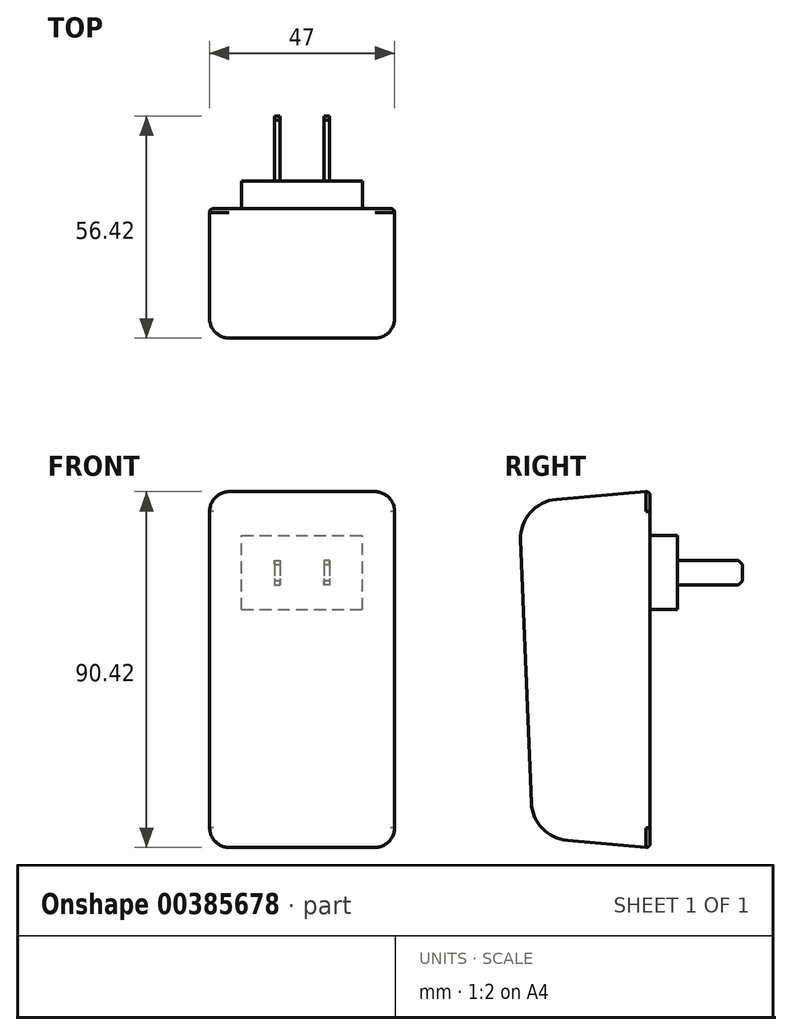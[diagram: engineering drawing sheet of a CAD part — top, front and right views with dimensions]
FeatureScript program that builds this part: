
annotation { "Feature Type Name" : "Feature", "Feature Type Description" : "" }
export const myFeature = defineFeature(function(context is Context, id is Id, definition is map)
    precondition{}
    {
        {
            var Q0;
            Q0=qCreatedBy(makeId("Right.planeOp"),FACE);
            var sketch = newSketch(context, id + "F0", { "sketchPlane" : qUnion([Q0])});
            skLineSegment(sketch, "E0", {"start": v(0, 90.6) * mm, "end": v(0, 0) * mm});
            skLineSegment(sketch, "E1", {"start": v(0, 90.6) * mm, "end": v(-33.3, 87.73) * mm});
            skLineSegment(sketch, "E2", {"start": v(-33.3, 87.73) * mm, "end": v(-29.8, 2.66) * mm});
            skLineSegment(sketch, "E3", {"start": v(-29.8, 2.66) * mm, "end": v(0, 0) * mm});
            skSolve(sketch);
        }
        {
            var Q0;
            Q0 = qSketchRegion(id + "F0", true);
            extrude(context, id + "F1", {"entities" : qUnion([Q0]), "depth" : 47 * mm, "symmetric" : true});
        }
        {
            var Q0;
            Q0=qCreatedBy(makeId("Front.planeOp"),FACE);
            var sketch = newSketch(context, id + "F2", { "sketchPlane" : qUnion([Q0])});
            skLineSegment(sketch, "E4", {"start": v(0, 0) * mm, "end": v(0, 19.9) * mm, "construction": true});
            skLineSegment(sketch, "E5.bottom", {"start": v(-15.37, 60.55) * mm, "end": v(15.37, 60.55) * mm});
            skLineSegment(sketch, "E5.top", {"start": v(-15.38, 79.35) * mm, "end": v(15.37, 79.35) * mm});
            skLineSegment(sketch, "E5.left", {"start": v(-15.37, 60.55) * mm, "end": v(-15.38, 79.35) * mm});
            skLineSegment(sketch, "E5.right", {"start": v(15.37, 60.55) * mm, "end": v(15.37, 79.35) * mm});
            skPoint(sketch, "E5.middle", {"position": v(0, 69.95) * mm});
            skLineSegment(sketch, "E6.bottom", {"start": v(-6.97, 73.05) * mm, "end": v(-5.57, 73.05) * mm});
            skLineSegment(sketch, "E6.top", {"start": v(-6.96, 66.84) * mm, "end": v(-5.57, 66.84) * mm});
            skLineSegment(sketch, "E6.left", {"start": v(-6.97, 73.05) * mm, "end": v(-6.97, 66.84) * mm});
            skLineSegment(sketch, "E6.right", {"start": v(-5.57, 73.05) * mm, "end": v(-5.57, 66.84) * mm});
            skPoint(sketch, "E6.middle", {"position": v(-6.26, 69.95) * mm});
            skLineSegment(sketch, "E7.MirrorCS", {"start": v(5.57, 73.05) * mm, "end": v(5.57, 66.84) * mm});
            skLineSegment(sketch, "E8.MirrorCS", {"start": v(6.96, 73.05) * mm, "end": v(6.96, 66.84) * mm});
            skLineSegment(sketch, "E9.MirrorCS", {"start": v(6.96, 66.84) * mm, "end": v(5.57, 66.84) * mm});
            skLineSegment(sketch, "E10.MirrorCS", {"start": v(6.97, 73.05) * mm, "end": v(5.57, 73.05) * mm});
            skPoint(sketch, "E11.MirrorP", {"position": v(6.26, 69.95) * mm});
            skSolve(sketch);
        }
        {
            var Q0;
            Q0=makeQuery(id+"F2.imprint","IMPRINT",FACE,{"disambiguationData":[TD([[makeQuery(id+"F2.imprint","IMPRINT",EDGE,{"derivedFrom":sQuery(id+"F2.wireOp",EDGE,"E7.MirrorCS")}),1.0]])]});
            var Q1;
            Q1=makeQuery(id+"F2.imprint","IMPRINT",FACE,{"disambiguationData":[TD([[makeQuery(id+"F2.imprint","IMPRINT",EDGE,{"derivedFrom":sQuery(id+"F2.wireOp",EDGE,"E6.bottom")}),-1.0]])]});
            var Q2;
            Q2=makeQuery(id+"F2.imprint","IMPRINT",FACE,{"disambiguationData":[TD([[makeQuery(id+"F2.imprint","IMPRINT",EDGE,{"derivedFrom":sQuery(id+"F2.wireOp",EDGE,"E5.bottom")}),1.0]])]});
            extrude(context, id + "F3", {"entities" : qUnion([Q0, Q1, Q2]), "operationType" : NewBodyOperationType.ADD, "oppositeDirection" : true, "depth" : 7 * mm});
        }
        {
            var Q0;
            Q0=makeQuery(id+"F2.imprint","IMPRINT",FACE,{"disambiguationData":[TD([[makeQuery(id+"F2.imprint","IMPRINT",EDGE,{"derivedFrom":sQuery(id+"F2.wireOp",EDGE,"E6.bottom")}),-1.0]])]});
            var Q1;
            Q1=makeQuery(id+"F2.imprint","IMPRINT",FACE,{"disambiguationData":[TD([[makeQuery(id+"F2.imprint","IMPRINT",EDGE,{"derivedFrom":sQuery(id+"F2.wireOp",EDGE,"E7.MirrorCS")}),1.0]])]});
            extrude(context, id + "F4", {"entities" : qUnion([Q0, Q1]), "operationType" : NewBodyOperationType.ADD, "oppositeDirection" : true, "depth" : 23.5 * mm});
        }
        {
            var Q0;
            Q0=makeQuery(id+"F1.opExtrude","SWEPT_EDGE",EDGE,{"disambiguationData":[OSD([sQuery(id+"F0.wireOp",EDGE,"E1"),sQuery(id+"F0.wireOp",EDGE,"E2")])]});
            var Q1;
            Q1=makeQuery(id+"F1.opExtrude","SWEPT_EDGE",EDGE,{"disambiguationData":[OSD([sQuery(id+"F0.wireOp",EDGE,"E2"),sQuery(id+"F0.wireOp",EDGE,"E3")])]});
            fillet(context, id + "F5", {"entities" : qUnion([Q0, Q1]), "radius" : 10 * mm, "tangentPropagation" : true, "allowEdgeOverflow" : false});
        }
        {
            var Q0;
            Q0=makeQuery(id+"F1.opExtrude","CAP_EDGE",EDGE,{"disambiguationData":[OSD([sQuery(id+"F0.wireOp",EDGE,"E2")])],"isStart":false});
            var Q1;
            Q1=makeQuery(id+"F1.opExtrude","CAP_EDGE",EDGE,{"disambiguationData":[OSD([sQuery(id+"F0.wireOp",EDGE,"E2")])],"isStart":true});
            fillet(context, id + "F6", {"entities" : qUnion([Q0, Q1]), "radius" : 5 * mm, "tangentPropagation" : true, "allowEdgeOverflow" : false});
        }
        {
            var Q0;
            Q0=makeQuery(id+"F1.opExtrude","CAP_EDGE",EDGE,{"disambiguationData":[OSD([sQuery(id+"F0.wireOp",EDGE,"E0")])],"isStart":false});
            fillet(context, id + "F7", {"entities" : qUnion([Q0]), "radius" : 1 * mm, "tangentPropagation" : true, "allowEdgeOverflow" : false});
        }
        {
            var Q0;
            Q0=makeQuery(id+"F4.opExtrude","CAP_EDGE",EDGE,{"disambiguationData":[OSD([sQuery(id+"F2.wireOp",EDGE,"E6.bottom")])],"isStart":false});
            var Q1;
            Q1=makeQuery(id+"F4.opExtrude","CAP_EDGE",EDGE,{"disambiguationData":[OSD([sQuery(id+"F2.wireOp",EDGE,"E6.top")])],"isStart":false});
            var Q2;
            Q2=makeQuery(id+"F4.opExtrude","CAP_EDGE",EDGE,{"disambiguationData":[OSD([sQuery(id+"F2.wireOp",EDGE,"E10.MirrorCS")])],"isStart":false});
            var Q3;
            Q3=makeQuery(id+"F4.opExtrude","CAP_EDGE",EDGE,{"disambiguationData":[OSD([sQuery(id+"F2.wireOp",EDGE,"E9.MirrorCS")])],"isStart":false});
            chamfer(context, id + "F8", {"entities" : qUnion([Q0, Q1, Q2, Q3]), "width" : 1 * mm, "tangentPropagation" : true});
        }
    });
